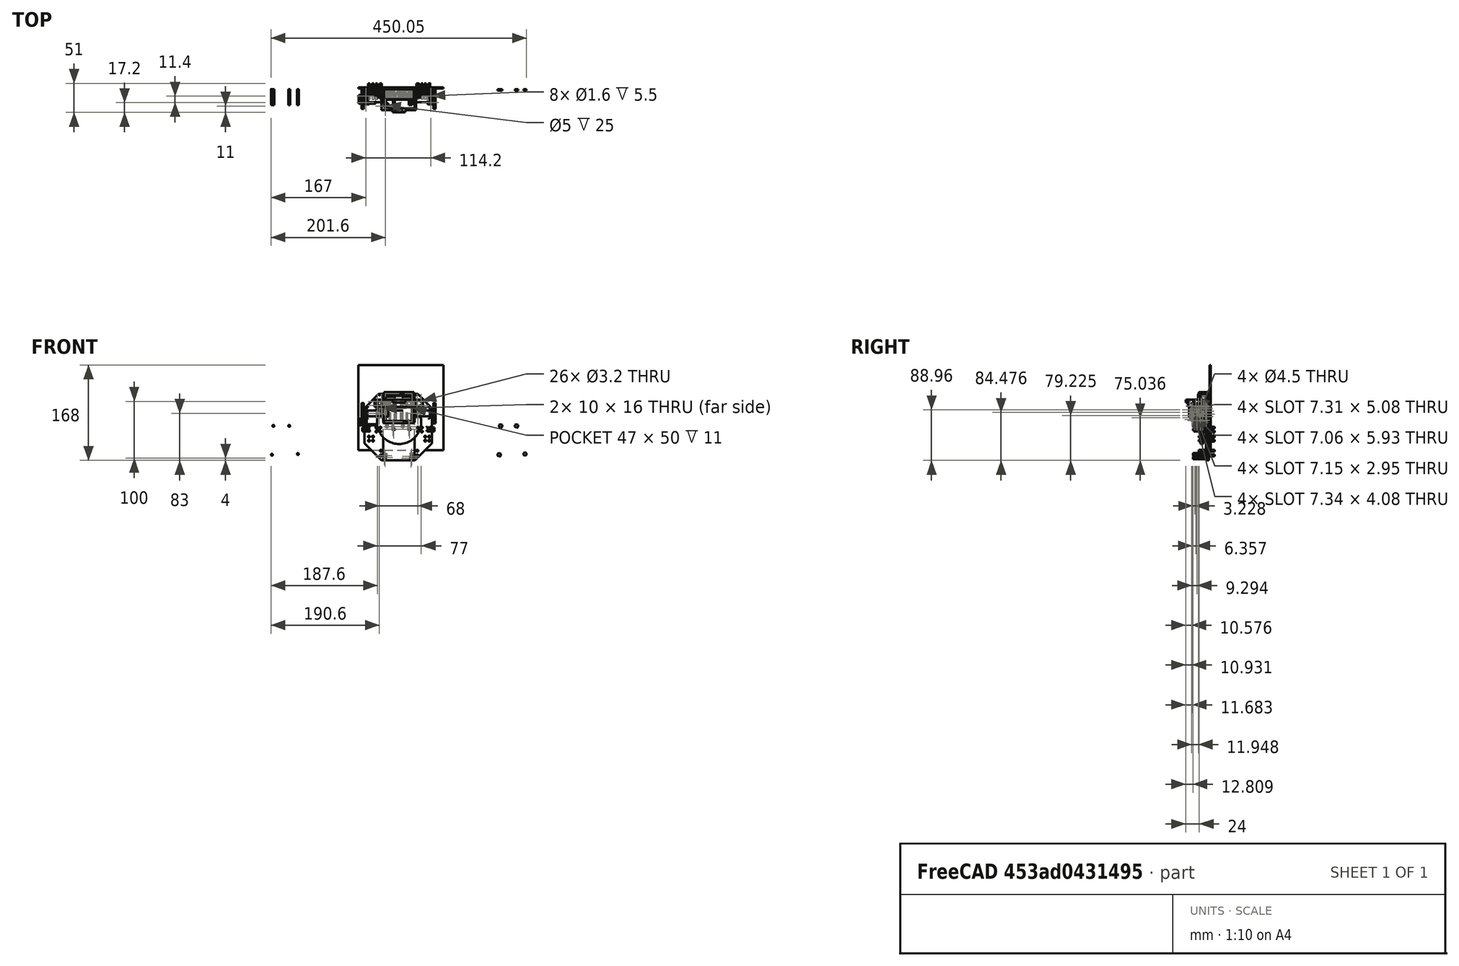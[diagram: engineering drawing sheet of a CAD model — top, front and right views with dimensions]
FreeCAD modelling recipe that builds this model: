
FCSTD DOCUMENT  (FreeCAD 0.16R6712 (Git))
Label: 5028.4 Frank
License: All rights reserved
LicenseURL: http://en.wikipedia.org/wiki/All_rights_reserved
objects: Part::Cylinder×127, Part::Box×74, Part::Cut×71, Part::Fuse×69, Part::Feature×37, Part::MultiFuse×36, Part::Fillet×16, Part::Mirroring×14, Part::Chamfer×12, Part::Cone×8, Part::Compound×3, Part::Torus×2, App::DocumentObjectGroup×1
note: 469 computed .brp shape members not serialized (recipe doc carries the construction recipe); baked Part::Feature solids carry a one-line shape summary decoded from their .brp

FEATURE [Part::Cylinder] Cylinder
  Angle = 360
  Height = 30
  Radius = 7
FEATURE [Part::Cylinder] Cylinder001
  Angle = 360
  Height = 19
  Placement = pos=(0,0,30) rot=(0,0,1;0rad)
  Radius = 7
FEATURE [Part::Cylinder] Cylinder002
  Angle = 360
  Height = 1.8
  Placement = pos=(0,0,49) rot=(0,0,1;0rad)
  Radius = 2.5
FEATURE [Part::Compound] Compound
  Links = -> [Cylinder,Cylinder002,Cylinder001]
FEATURE [Part::Cylinder] Cylinder003
  Angle = 360
  Height = 30
  Radius = 7
FEATURE [Part::Cylinder] Cylinder004
  Angle = 360
  Height = 19
  Placement = pos=(0,0,30) rot=(0,0,1;0rad)
  Radius = 7
FEATURE [Part::Cylinder] Cylinder005
  Angle = 360
  Height = 1.8
  Placement = pos=(0,0,49) rot=(0,0,1;0rad)
  Radius = 2.5
FEATURE [Part::Compound] Compound001
  Links = -> [Cylinder003,Cylinder005,Cylinder004]
  Placement = pos=(14.5,0,50) rot=(1,0,0;3.14159rad)
FEATURE [Part::Cylinder] Cylinder006
  Angle = 360
  Height = 30
  Radius = 7
FEATURE [Part::Cylinder] Cylinder007
  Angle = 360
  Height = 19
  Placement = pos=(0,0,30) rot=(0,0,1;0rad)
  Radius = 7
FEATURE [Part::Cylinder] Cylinder008
  Angle = 360
  Height = 1.8
  Placement = pos=(0,0,49) rot=(0,0,1;0rad)
  Radius = 2.5
FEATURE [Part::Compound] Compound002
  Links = -> [Cylinder006,Cylinder008,Cylinder007]
  Placement = pos=(29,0,0) rot=(0,0,1;0rad)
FEATURE [Part::Box] Box  label="Cube"
  Height = 50
  Length = 47
  Placement = pos=(-9,-8,0) rot=(0,0,1;0rad)
  Width = 12
FEATURE [Part::Box] Box001  label="Cube001"
  Height = 55
  Length = 53
  Placement = pos=(-12,-8,-2.5) rot=(0,0,1;0rad)
  Width = 11
FEATURE [Part::Cylinder] Cylinder009
  Angle = 360
  Height = 50
  Radius = 7
FEATURE [Part::Cylinder] Cylinder010
  Angle = 360
  Height = 50
  Placement = pos=(14.5,0,0) rot=(0,0,1;0rad)
  Radius = 7
FEATURE [Part::Cut] Cut
  Base = -> Box001
  Tool = -> Box
FEATURE [Part::Box] Box002  label="Cube002"
  Height = 55
  Length = 53
  Placement = pos=(-12,3,-2.5) rot=(0,0,1;0rad)
  Width = 7
FEATURE [Part::Fuse] Fusion
  Base = -> Cut
  Tool = -> Box002
FEATURE [Part::Cut] Cut001  label="No idea why this is here...."
  Base = -> Fusion
  Tool = -> Cylinder009
FEATURE [Part::Cylinder] Cylinder011
  Angle = 360
  Height = 50
  Placement = pos=(29,0,0) rot=(0,0,1;0rad)
  Radius = 7
FEATURE [Part::Box] Box003  label="Cube003"
  Height = 5
  Length = 2
  Placement = pos=(28,-9,-2) rot=(0,0,1;0rad)
  Width = 12
FEATURE [Part::Box] Box004  label="Cube004"
  Height = 5
  Length = 2
  Placement = pos=(18.5,-9,46) rot=(0,0,1;0rad)
  Width = 12
FEATURE [Part::Box] Box005  label="Cube005"
  Height = 5
  Length = 2
  Placement = pos=(-2,-9,46) rot=(0,0,1;0rad)
  Width = 12
FEATURE [Part::Box] Box006  label="Cube006"
  Height = 5
  Length = 3
  Placement = pos=(35,-9,-4) rot=(0,0,1;0rad)
  Width = 12
FEATURE [Part::Cut] Cut008
FEATURE [Part::Torus] Torus001
  Angle1 = -180
  Angle2 = 180
  Angle3 = 360
  Placement = pos=(0,0,2) rot=(0,0,1;0rad)
  Radius1 = 19
  Radius2 = 1.5
FEATURE [Part::Cut] Cut009  label="wheel2"
  Base = -> Cut008
  Placement = pos=(75,-7,15) rot=(0,1,0;1.5708rad)
  Tool = -> Torus001
FEATURE [Part::Torus] Torus
  Angle1 = -180
  Angle2 = 180
  Angle3 = 360
  Placement = pos=(0,0,2) rot=(0,0,1;0rad)
  Radius1 = 19
  Radius2 = 1.5
FEATURE [Part::Cut] Cut010
FEATURE [Part::Cut] Cut011  label="wheel1"
  Base = -> Cut010
  Placement = pos=(-51,-7,15) rot=(0,1,0;1.5708rad)
  Tool = -> Torus
FEATURE [Part::Fuse] Fusion003
FEATURE [Part::Cylinder] Cylinder012
  Angle = 360
  Height = 10
  Placement = pos=(5,-4.5,0) rot=(0,1,0;1.5708rad)
  Radius = 0.8
FEATURE [Part::Fuse] Fusion048  label="right-motor001"
  Base = -> Cylinder012
  Placement = pos=(-51,-7,15) rot=(0,0,1;0rad)
  Tool = -> Fusion003
FEATURE [Part::Fuse] Fusion049
FEATURE [Part::Cylinder] Cylinder013
  Angle = 360
  Height = 10
  Placement = pos=(5,-4.5,0) rot=(0,1,0;1.5708rad)
  Radius = 0.8
FEATURE [Part::Fuse] Fusion050  label="left-motor001"
  Base = -> Cylinder013
  Placement = pos=(79,-7,15) rot=(0,0,1;3.14159rad)
  Tool = -> Fusion049
FEATURE [Part::Box] Box007  label="Cube007"
  Height = 5
  Length = 2
  Placement = pos=(37.5,-9,46) rot=(0,0,1;0rad)
  Width = 12
FEATURE [Part::Box] Box008  label="Cube008"
  Height = 5
  Length = 2
  Placement = pos=(8,-9,-2) rot=(0,0,1;0rad)
  Width = 12
FEATURE [Part::Box] Box009  label="The Ground"
  Height = 150
  Length = 150
  Placement = pos=(-57,11,-50) rot=(0,0,1;0rad)
  Width = 2
FEATURE [Part::Box] Box010  label="Motor Mount Left"
  Height = 16
  Length = 4
  Placement = pos=(69,-13,7) rot=(0,0,1;0rad)
  Width = 20
FEATURE [Part::Box] Box011  label="Motor Mount Right"
  Height = 16
  Length = 4
  Placement = pos=(-46,-13,7) rot=(0,0,1;0rad)
  Width = 20
FEATURE [Part::Box] Box012  label="Motor Support Right"
  Height = 16
  Length = 10
  Placement = pos=(-25,-1,7) rot=(0,0,1;0rad)
  Width = 8
FEATURE [Part::Box] Box013  label="Motor Support Left"
  Height = 16
  Length = 10
  Placement = pos=(43,-1,7) rot=(0,0,1;0rad)
  Width = 8
FEATURE [Part::Cylinder] Cylinder014
  Angle = 360
  Height = 28
  Placement = pos=(40.7,0,-10.3) rot=(1,0,0;1.5708rad)
  Radius = 1.6
FEATURE [Part::Cylinder] Cylinder015
  Angle = 360
  Height = 28
  Placement = pos=(-2.4,0,-59.8) rot=(1,0,0;1.5708rad)
  Radius = 1.6
FEATURE [Part::Cylinder] Cylinder016
  Angle = 360
  Height = 28
  Placement = pos=(-5,0,-9) rot=(1,0,0;1.5708rad)
  Radius = 1.6
FEATURE [Part::Cylinder] Cylinder017
  Angle = 360
  Height = 28
  Placement = pos=(25.5,0,-59.8) rot=(1,0,0;1.5708rad)
  Radius = 1.6
FEATURE [Part::Fuse] Fusion051
  Base = -> Cylinder015
  Tool = -> Cylinder016
FEATURE [Part::Fuse] Fusion052
  Base = -> Cylinder014
  Tool = -> Cylinder017
FEATURE [Part::Fuse] Fusion053  label="Screw holes on Arduino Duo"
  Base = -> Fusion051
  Tool = -> Fusion052
FEATURE [Part::Mirroring] Part__Mirroring  label="XXXXXScrew holes on Arduino Duo (Mirror #1)"
  Base = (0,0,0)
  Normal = (0,0,1)
  Placement = pos=(-204,10,-67) rot=(0,0,1;0rad)
  Source = -> Fusion053
FEATURE [Part::Box] Box014  label="Not used Cube"
  Height = 10
  Length = 10
  Placement = pos=(-1,4,-5.85) rot=(0,0,1;0rad)
  Width = 10
FEATURE [Part::Box] Box015  label="Cube014 Arduino Support cube"
  Height = 67
  Length = 55
  Placement = pos=(-13,5,-68) rot=(0,0,1;0rad)
  Width = 5
FEATURE [Part::Cylinder] Cylinder018
  Angle = 360
  Height = 5
  Placement = pos=(15,0,0) rot=(1,0,0;1.5708rad)
  Radius = 39
FEATURE [Part::Cut] Cut014  label="M3 Nut"
  Base = -> Cut001
  Placement = pos=(-6.4,10,-7.2) rot=(1,0,0;1.5708rad)
  Tool = -> Cylinder001
FEATURE [Part::Cut] Cut015  label="M3 Nut001"
  Base = -> Cut001
  Placement = pos=(21.5,10,-7.2) rot=(1,0,0;1.5708rad)
  Tool = -> Cylinder001
FEATURE [Part::Cut] Cut016  label="M3 Nut002"
  Base = -> Cut001
  Placement = pos=(36.7,10,-56.7) rot=(1,0,0;1.5708rad)
  Tool = -> Cylinder001
FEATURE [Part::Cut] Cut017  label="M3 Nut003"
  Base = -> Cut001
  Placement = pos=(-9,10,-58) rot=(1,0,0;1.5708rad)
  Tool = -> Cylinder001
FEATURE [Part::Cut] Cut018
  Base = -> Cut
  Placement = pos=(-9,10,-58) rot=(1,0,0;1.5708rad)
  Tool = -> Box006
FEATURE [Part::Cut] Cut019
  Base = -> Cut
  Placement = pos=(36.7,10,-56.7) rot=(1,0,0;1.5708rad)
  Tool = -> Box006
FEATURE [Part::Cut] Cut020
  Base = -> Cut
  Placement = pos=(-6.4,10,-7.2) rot=(1,0,0;1.5708rad)
  Tool = -> Box006
FEATURE [Part::Cut] Cut021
  Base = -> Cut
  Placement = pos=(21.5,10,-7.2) rot=(1,0,0;1.5708rad)
  Tool = -> Box006
FEATURE [Part::MultiFuse] Fusion054  label="XXXXXHex Holes"
  Placement = pos=(200,0,0) rot=(0,0,1;0rad)
  Shapes = -> [Cut018,Cut021,Cut019,Cut020]
FEATURE [Part::Box] Box016  label="Cube015"
  Height = 117
  Length = 33
  Placement = pos=(-46,7,-68) rot=(0,0,1;0rad)
  Width = 3
FEATURE [Part::Box] Box017  label="Cube016"
  Height = 117
  Length = 31
  Placement = pos=(42,7,-68) rot=(0,0,1;0rad)
  Width = 3
FEATURE [Part::Cylinder] Cylinder019
  Angle = 360
  Height = 28
  Placement = pos=(48,20,-10) rot=(1,0,0;1.5708rad)
  Radius = 1.6
FEATURE [Part::Cylinder] Cylinder020
  Angle = 360
  Height = 28
  Placement = pos=(47,20,-51) rot=(1,0,0;1.5708rad)
  Radius = 1.6
FEATURE [Part::Cylinder] Cylinder021
  Angle = 360
  Height = 28
  Placement = pos=(48,20,-17) rot=(1,0,0;1.5708rad)
  Radius = 1.6
FEATURE [Part::Cylinder] Cylinder022
  Angle = 360
  Height = 28
  Placement = pos=(47,20,-59) rot=(1,0,0;1.5708rad)
  Radius = 1.6
FEATURE [Part::Cylinder] Cylinder023
  Angle = 360
  Height = 28
  Placement = pos=(55,20,-17) rot=(1,0,0;1.5708rad)
  Radius = 1.6
FEATURE [Part::Cylinder] Cylinder024
  Angle = 360
  Height = 28
  Placement = pos=(55,20,-10) rot=(1,0,0;1.5708rad)
  Radius = 1.6
FEATURE [Part::MultiFuse] Fusion055
  Shapes = -> [Cylinder021,Cylinder023,Cylinder024,Cylinder019]
FEATURE [Part::MultiFuse] Fusion056
  Placement = pos=(13,0,-16) rot=(0,0,1;0rad)
  Shapes = -> [Cylinder021,Cylinder023,Cylinder024,Cylinder019]
FEATURE [Part::MultiFuse] Fusion057  label="Mount holes top left"
  Placement = pos=(-1,0,46) rot=(0,0,1;0rad)
  Shapes = -> [Cylinder021,Cylinder023,Cylinder024,Cylinder019]
FEATURE [Part::MultiFuse] Fusion058  label="Mount holes top right"
  Placement = pos=(-71,0,46) rot=(0,0,1;0rad)
  Shapes = -> [Cylinder021,Cylinder023,Cylinder024,Cylinder019]
FEATURE [Part::MultiFuse] Fusion059
  Shapes = -> [Cylinder022,Cylinder020,Fusion055,Fusion056]
FEATURE [Part::Mirroring] Part__Mirroring001  label="Mount holes bottom right"
  Base = (0,0,0)
  Normal = (1,0,0)
  Placement = pos=(30,0,0) rot=(0,0,1;0rad)
  Source = -> Fusion059
FEATURE [Part::Cylinder] Cylinder025
  Angle = 360
  Height = 28
  Placement = pos=(48,20,-10) rot=(1,0,0;1.5708rad)
  Radius = 1.6
FEATURE [Part::Cylinder] Cylinder026
  Angle = 360
  Height = 28
  Placement = pos=(47,20,-51) rot=(1,0,0;1.5708rad)
  Radius = 1.6
FEATURE [Part::Cylinder] Cylinder027
  Angle = 360
  Height = 28
  Placement = pos=(48,20,-17) rot=(1,0,0;1.5708rad)
  Radius = 1.6
FEATURE [Part::Cylinder] Cylinder028
  Angle = 360
  Height = 28
  Placement = pos=(47,20,-59) rot=(1,0,0;1.5708rad)
  Radius = 1.6
FEATURE [Part::Cylinder] Cylinder029
  Angle = 360
  Height = 28
  Placement = pos=(55,20,-17) rot=(1,0,0;1.5708rad)
  Radius = 1.6
FEATURE [Part::Cylinder] Cylinder030
  Angle = 360
  Height = 28
  Placement = pos=(55,20,-10) rot=(1,0,0;1.5708rad)
  Radius = 1.6
FEATURE [Part::MultiFuse] Fusion060
  Shapes = -> [Cylinder027,Cylinder029,Cylinder030,Cylinder025]
FEATURE [Part::MultiFuse] Fusion061
  Placement = pos=(13,0,-16) rot=(0,0,1;0rad)
  Shapes = -> [Cylinder027,Cylinder029,Cylinder030,Cylinder025]
FEATURE [Part::MultiFuse] Fusion062  label="Mount holes bottom left"
  Shapes = -> [Cylinder028,Cylinder026,Fusion060,Fusion061]
FEATURE [Part::Cylinder] Cylinder031  label="Cylinder127"
  Angle = 360
  Height = 10
  Placement = pos=(0,18,29) rot=(0,0,1;0rad)
  Radius = 2.25
FEATURE [Part::Cylinder] Cylinder032  label="Cylinder128"
  Angle = 360
  Height = 10
  Placement = pos=(4.5,18,32) rot=(0,0,1;0rad)
  Radius = 1
FEATURE [Part::Cylinder] Cylinder033  label="Cylinder129"
  Angle = 360
  Height = 10
  Placement = pos=(-4.5,18,32) rot=(0,0,1;0rad)
  Radius = 1
FEATURE [Part::Fuse] Fusion009  label="Mounting Screw Holes"
  Base = -> Cylinder032
  Tool = -> Cylinder033
FEATURE [Part::Fuse] Fusion071  label="Motor Holes Left"
  Base = -> Cylinder031
  Placement = pos=(37,-7,-3) rot=(0.57735,0.57735,0.57735;2.0944rad)
  Tool = -> Fusion009
FEATURE [Part::Cylinder] Cylinder034  label="Cylinder130"
  Angle = 360
  Height = 10
  Placement = pos=(0,18,29) rot=(0,0,1;0rad)
  Radius = 2.25
FEATURE [Part::Cylinder] Cylinder035  label="Cylinder131"
  Angle = 360
  Height = 10
  Placement = pos=(4.5,18,32) rot=(0,0,1;0rad)
  Radius = 1
FEATURE [Part::Cylinder] Cylinder036  label="Cylinder132"
  Angle = 360
  Height = 10
  Placement = pos=(-4.5,18,32) rot=(0,0,1;0rad)
  Radius = 1
FEATURE [Part::Fuse] Fusion072  label="Mounting Screw Holes001"
  Base = -> Cylinder035
  Tool = -> Cylinder036
FEATURE [Part::Fuse] Fusion073  label="Motor Holes Right"
  Base = -> Cylinder034
  Placement = pos=(-79,-7,-3) rot=(0.57735,0.57735,0.57735;2.0944rad)
  Tool = -> Fusion072
FEATURE [Part::Cylinder] Cylinder037  label="Cylinder133"
  Angle = 360
  Height = 28
  Placement = pos=(40.7,0,-10.3) rot=(1,0,0;1.5708rad)
  Radius = 1.6
FEATURE [Part::Cylinder] Cylinder038  label="Cylinder134"
  Angle = 360
  Height = 28
  Placement = pos=(-2.4,0,-59.8) rot=(1,0,0;1.5708rad)
  Radius = 1.6
FEATURE [Part::Cylinder] Cylinder039  label="Cylinder135"
  Angle = 360
  Height = 28
  Placement = pos=(-5,0,-9) rot=(1,0,0;1.5708rad)
  Radius = 1.6
FEATURE [Part::Cylinder] Cylinder040  label="Cylinder136"
  Angle = 360
  Height = 28
  Placement = pos=(25.5,0,-59.8) rot=(1,0,0;1.5708rad)
  Radius = 1.6
FEATURE [Part::Fuse] Fusion074
  Base = -> Cylinder038
  Tool = -> Cylinder039
FEATURE [Part::Fuse] Fusion075
  Base = -> Cylinder037
  Tool = -> Cylinder040
FEATURE [Part::Fuse] Fusion076  label="Screw holes on Arduino Duo001"
  Base = -> Fusion074
  Tool = -> Fusion075
FEATURE [Part::Mirroring] Part__Mirroring002  label="Screw holes on Arduino Duo (Mirror #1)001"
  Base = (0,0,0)
  Normal = (0,0,1)
  Placement = pos=(-4,10,-67) rot=(0,0,1;0rad)
  Source = -> Fusion076
FEATURE [Part::Mirroring] Part__Mirroring003  label="Screw holes on Arduino Duo (Mirror #1)001 (Mirror #4)"
  Base = (0,0,0)
  Normal = (1,0,0)
  Placement = pos=(27,0,-6) rot=(0,0,1;0rad)
  Source = -> Part__Mirroring002
FEATURE [Part::Box] Box018  label="Cube017"
  Height = 50
  Length = 47
  Placement = pos=(-9,-8,0) rot=(0,0,1;0rad)
  Width = 12
FEATURE [Part::Box] Box019  label="Cube018"
  Height = 55
  Length = 53
  Placement = pos=(-12,-8,-2.5) rot=(0,0,1;0rad)
  Width = 11
FEATURE [Part::Cut] Cut031
  Base = -> Box019
  Tool = -> Box018
FEATURE [Part::Box] Box020  label="Cube019"
  Height = 5
  Length = 3
  Placement = pos=(35,-9,-4) rot=(0,0,1;0rad)
  Width = 12
FEATURE [Part::Cut] Cut032
  Base = -> Cut031
  Placement = pos=(-9,10,-58) rot=(1,0,0;1.5708rad)
  Tool = -> Box020
FEATURE [Part::Cut] Cut033
  Base = -> Cut031
  Placement = pos=(36.7,10,-56.7) rot=(1,0,0;1.5708rad)
  Tool = -> Box020
FEATURE [Part::Cut] Cut034
  Base = -> Cut031
  Placement = pos=(-6.4,10,-7.2) rot=(1,0,0;1.5708rad)
  Tool = -> Box020
FEATURE [Part::Cut] Cut035
  Base = -> Cut031
  Placement = pos=(21.5,10,-7.2) rot=(1,0,0;1.5708rad)
  Tool = -> Box020
FEATURE [Part::MultiFuse] Fusion077
  Shapes = -> [Cut032,Cut035,Cut033,Cut034]
FEATURE [Part::Mirroring] Part__Mirroring004  label="Hex Holes"
  Base = (0,0,0)
  Normal = (1,0,0)
  Placement = pos=(27,0,-6) rot=(0,0,1;0rad)
  Source = -> Fusion077
FEATURE [Part::Box] Box021  label="Cube020"
  Height = 13
  Length = 61
  Placement = pos=(-16,-27,26) rot=(0,0,1;0rad)
  Width = 34
FEATURE [Part::Box] Box022  label="Cube021"
  Height = 13
  Length = 12
  Placement = pos=(45,4,26) rot=(0,0,1;0rad)
  Width = 3
FEATURE [Part::Box] Box023  label="Cube022"
  Height = 13
  Length = 12
  Placement = pos=(-28,4,26) rot=(0,0,1;0rad)
  Width = 3
FEATURE [Part::Box] Box024  label="Cube023"
  Height = 13
  Length = 55
  Placement = pos=(-13,-24,26) rot=(0,0,1;0rad)
  Width = 31
FEATURE [Part::Cylinder] Cylinder041  label="Cylinder137"
  Angle = 360
  Height = 28
  Placement = pos=(54,20,29) rot=(1,0,0;1.5708rad)
  Radius = 1.6
FEATURE [Part::Cylinder] Cylinder042  label="Cylinder138"
  Angle = 360
  Height = 28
  Placement = pos=(54,20,36) rot=(1,0,0;1.5708rad)
  Radius = 1.6
FEATURE [Part::Cylinder] Cylinder043  label="Cylinder139"
  Angle = 360
  Height = 28
  Placement = pos=(-23,20,29) rot=(1,0,0;1.5708rad)
  Radius = 1.6
FEATURE [Part::Cylinder] Cylinder044  label="Cylinder140"
  Angle = 360
  Height = 28
  Placement = pos=(-23,20,36) rot=(1,0,0;1.5708rad)
  Radius = 1.6
FEATURE [Part::Cylinder] Cylinder045  label="Cylinder141"
  Angle = 360
  Height = 10
  Placement = pos=(36,-17.25,32.5) rot=(0,1,0;1.5708rad)
  Radius = 2.5
FEATURE [Part::Cut] Cut037
  Base = -> Box021
  Tool = -> Box024
FEATURE [Part::Cut] Cut038
  Base = -> Cut037
  Tool = -> Cylinder045
FEATURE [Part::Box] Box025  label="Cube024"
  Height = 5
  Length = 22
  Placement = pos=(3.5,-31,34) rot=(0,0,1;0rad)
  Width = 4
FEATURE [Part::Cylinder] Cylinder046  label="Cylinder142"
  Angle = 360
  Height = 10
  Placement = pos=(20.75,-29,30) rot=(0,0,1;0rad)
  Radius = 0.85
FEATURE [Part::Cylinder] Cylinder047  label="Cylinder143"
  Angle = 360
  Height = 10
  Placement = pos=(8.25,-29,40) rot=(1,0,0;3.14159rad)
  Radius = 0.85
FEATURE [Part::Fuse] Fusion078
  Base = -> Cylinder046
  Tool = -> Cylinder047
FEATURE [Part::Cut] Cut039
  Base = -> Box025
  Tool = -> Fusion078
FEATURE [Part::Fuse] Fusion079
  Base = -> Cut038
  Tool = -> Cut039
FEATURE [Part::Fuse] Fusion080
  Base = -> Cylinder043
  Tool = -> Cylinder044
FEATURE [Part::Fuse] Fusion081
  Base = -> Cylinder041
  Tool = -> Cylinder042
FEATURE [Part::Fuse] Fusion082
  Base = -> Box023
  Tool = -> Fusion079
FEATURE [Part::Fuse] Fusion083
  Base = -> Box022
  Tool = -> Fusion082
FEATURE [Part::Cut] Cut040
  Base = -> Fusion083
  Tool = -> Fusion081
FEATURE [Part::Cut] Cut041  label="Switch Bracket"
  Base = -> Cut040
  Tool = -> Fusion080
FEATURE [Part::Cylinder] Cylinder048  label="Cylinder144"
  Angle = 360
  Height = 28
  Placement = pos=(-23,20,29) rot=(1,0,0;1.5708rad)
  Radius = 1.6
FEATURE [Part::Cylinder] Cylinder049  label="Cylinder145"
  Angle = 360
  Height = 28
  Placement = pos=(-23,20,36) rot=(1,0,0;1.5708rad)
  Radius = 1.6
FEATURE [Part::Fuse] Fusion084
  Base = -> Cylinder048
  Placement = pos=(1,0,0) rot=(0,0,1;0rad)
  Tool = -> Cylinder049
FEATURE [Part::Cylinder] Cylinder050  label="Cylinder146"
  Angle = 360
  Height = 28
  Placement = pos=(-23,20,29) rot=(1,0,0;1.5708rad)
  Radius = 1.6
FEATURE [Part::Cylinder] Cylinder051  label="Cylinder147"
  Angle = 360
  Height = 28
  Placement = pos=(-23,20,36) rot=(1,0,0;1.5708rad)
  Radius = 1.6
FEATURE [Part::Fuse] Fusion085
  Base = -> Cylinder050
  Placement = pos=(-1,0,0) rot=(0,0,1;0rad)
  Tool = -> Cylinder051
FEATURE [Part::Cut] Cut042
  Base = -> Cut041
  Tool = -> Fusion084
FEATURE [Part::Cut] Cut043  label="Switch Bracket001"
  Base = -> Cut042
  Tool = -> Fusion085
FEATURE [Part::Cylinder] Cylinder052  label="Cylinder148"
  Angle = 360
  Height = 42
  Radius = 4.8
FEATURE [Part::Cylinder] Cylinder053  label="Cylinder149"
  Angle = 360
  Height = 1.6
  Placement = pos=(0,0,42) rot=(0,0,1;0rad)
  Radius = 1.65
FEATURE [Part::Fuse] Fusion086
  Base = -> Cylinder052
  Placement = pos=(2,0,0) rot=(0,0,1;0rad)
  Tool = -> Cylinder053
FEATURE [Part::Cylinder] Cylinder054  label="Cylinder150"
  Angle = 360
  Height = 42
  Radius = 4.8
FEATURE [Part::Cylinder] Cylinder055  label="Cylinder151"
  Angle = 360
  Height = 1.6
  Placement = pos=(0,0,42) rot=(0,0,1;0rad)
  Radius = 1.65
FEATURE [Part::Fuse] Fusion087
  Base = -> Cylinder054
  Placement = pos=(12,0,0) rot=(0,0,1;0rad)
  Tool = -> Cylinder055
FEATURE [Part::Cylinder] Cylinder056  label="Cylinder152"
  Angle = 360
  Height = 42
  Radius = 4.8
FEATURE [Part::Cylinder] Cylinder057  label="Cylinder153"
  Angle = 360
  Height = 1.6
  Placement = pos=(0,0,42) rot=(0,0,1;0rad)
  Radius = 1.65
FEATURE [Part::Fuse] Fusion088
  Base = -> Cylinder056
  Placement = pos=(22,0,0) rot=(0,0,1;0rad)
  Tool = -> Cylinder057
FEATURE [Part::Cylinder] Cylinder058  label="Cylinder154"
  Angle = 360
  Height = 42
  Radius = 4.8
FEATURE [Part::Cylinder] Cylinder059  label="Cylinder155"
  Angle = 360
  Height = 1.6
  Placement = pos=(0,0,42) rot=(0,0,1;0rad)
  Radius = 1.65
FEATURE [Part::Fuse] Fusion089
  Base = -> Cylinder058
  Placement = pos=(32,0,0) rot=(0,0,1;0rad)
  Tool = -> Cylinder059
FEATURE [Part::Cylinder] Cylinder060  label="Cylinder156"
  Angle = 360
  Height = 42
  Radius = 4.8
FEATURE [Part::Cylinder] Cylinder061  label="Cylinder157"
  Angle = 360
  Height = 1.6
  Placement = pos=(0,0,42) rot=(0,0,1;0rad)
  Radius = 1.65
FEATURE [Part::Fuse] Fusion093
  Base = -> Cylinder060
  Placement = pos=(-8,0,0) rot=(0,0,1;0rad)
  Tool = -> Cylinder061
FEATURE [Part::MultiFuse] Fusion094  label="AAA Batts"
  Placement = pos=(2.5,0,2) rot=(0,0,1;0rad)
  Shapes = -> [Fusion093,Fusion086,Fusion087,Fusion088,Fusion089]
FEATURE [Part::Cylinder] Cylinder062  label="Cylinder158"
  Angle = 360
  Height = 10
  Radius = 17
FEATURE [Part::Cylinder] Cylinder063  label="Cylinder159"
  Angle = 360
  Height = 16
  Placement = pos=(0,0,-4) rot=(0,0,1;0rad)
  Radius = 10
FEATURE [Part::Cut] Cut044
  Base = -> Cylinder062
  Tool = -> Cylinder063
FEATURE [Part::Box] Box026  label="Cube025"
  Height = 20
  Length = 18
  Placement = pos=(0,0,-5) rot=(0,0,1;0rad)
  Width = 20
FEATURE [Part::Box] Box027  label="Cube026"
  Height = 20
  Length = 10
  Placement = pos=(0,0,-5) rot=(0,0,1;0.174533rad)
  Width = 20
FEATURE [Part::Cut] Cut045
  Base = -> Box027
  Tool = -> Box026
FEATURE [Part::Feature] Cut045001
  Placement = pos=(0,0,0) rot=(0,0,1;0.349066rad)
  shape: bbox 10 x 22.32 x 20 mm, 7 faces (baked)
FEATURE [Part::Feature] Cut045002
  Placement = pos=(0,0,0) rot=(0,0,1;0.698132rad)
  shape: bbox 15.32 x 20.52 x 20 mm, 7 faces (baked)
FEATURE [Part::Feature] Cut045003
  Placement = pos=(0,0,0) rot=(0,0,1;1.0472rad)
  shape: bbox 18.79 x 16.24 x 20 mm, 7 faces (baked)
FEATURE [Part::Feature] Cut045004
  Placement = pos=(0,0,0) rot=(0,0,1;1.39626rad)
  shape: bbox 20 x 10 x 20 mm, 7 faces (baked)
FEATURE [Part::Feature] Cut045005
  Placement = pos=(0,0,0) rot=(0,0,1;1.74533rad)
  shape: bbox 22.21 x 9.894 x 20 mm, 7 faces (baked)
FEATURE [Part::Feature] Cut045006
  Placement = pos=(0,0,0) rot=(0,0,1;2.0944rad)
  shape: bbox 21.75 x 12.86 x 20 mm, 7 faces (baked)
FEATURE [Part::Feature] Cut045007
  Placement = pos=(0,0,0) rot=(0,0,1;2.44346rad)
  shape: bbox 18.66 x 17.32 x 20 mm, 7 faces (baked)
FEATURE [Part::Feature] Cut045008
  Placement = pos=(0,0,0) rot=(0,0,1;2.79253rad)
  shape: bbox 13.32 x 19.7 x 20 mm, 7 faces (baked)
FEATURE [Part::Feature] Cut045009
  Placement = pos=(0,0,0) rot=(0,0,1;3.14159rad)
  shape: bbox 10.1 x 21.43 x 20 mm, 7 faces (baked)
FEATURE [Part::Feature] Cut045010
  Placement = pos=(0,0,0) rot=(0,0,1;3.49066rad)
  shape: bbox 10 x 22.32 x 20 mm, 7 faces (baked)
FEATURE [Part::Feature] Cut045011
  Placement = pos=(0,0,0) rot=(0,0,1;3.83972rad)
  shape: bbox 15.32 x 20.52 x 20 mm, 7 faces (baked)
FEATURE [Part::Feature] Cut045012
  Placement = pos=(0,0,0) rot=(0,0,1;4.18879rad)
  shape: bbox 18.79 x 16.24 x 20 mm, 7 faces (baked)
FEATURE [Part::Feature] Cut045013
  Placement = pos=(0,0,0) rot=(0,0,-1;1.74533rad)
  shape: bbox 20 x 10 x 20 mm, 7 faces (baked)
FEATURE [Part::Feature] Cut045014
  Placement = pos=(0,0,0) rot=(0,0,-1;1.39626rad)
  shape: bbox 22.21 x 9.894 x 20 mm, 7 faces (baked)
FEATURE [Part::Feature] Cut045015
  Placement = pos=(0,0,0) rot=(0,0,-1;1.0472rad)
  shape: bbox 21.75 x 12.86 x 20 mm, 7 faces (baked)
FEATURE [Part::Feature] Cut045016
  Placement = pos=(0,0,0) rot=(0,0,-1;0.698132rad)
  shape: bbox 18.66 x 17.32 x 20 mm, 7 faces (baked)
FEATURE [Part::Feature] Cut045017
  Placement = pos=(0,0,0) rot=(0,0,-1;0.349066rad)
  shape: bbox 13.32 x 19.7 x 20 mm, 7 faces (baked)
FEATURE [Part::MultiFuse] Fusion095
  Shapes = -> [Cut045001,Cut045008,Cut045010,Cut045009,Cut045005,Cut045003,Cut045006,Cut045002,Cut045004,Cut045007,Cut045016,Cut045017,Cut045011,Cut045012,Cut045013,Cut045014,Cut045015,Cut045]
FEATURE [Part::Cut] Cut045018
  Base = -> Cut044
  Placement = pos=(72,-7,15) rot=(0,1,0;1.5708rad)
  Tool = -> Fusion095
FEATURE [Part::Cut] Cut045019  label="Wheel with Spokes AB"
  Base = -> Cut009
  Tool = -> Cut045018
FEATURE [Part::Box] Box028  label="Cube027"
  Height = 5
  Length = 2
  Placement = pos=(37.5,-9,-2) rot=(0,0,1;0rad)
  Width = 12
FEATURE [Part::Box] Box029  label="Cube028"
  Height = 50
  Length = 47
  Placement = pos=(-9,-8,0) rot=(0,0,1;0rad)
  Width = 12
FEATURE [Part::Box] Box030  label="Cube029"
  Height = 55
  Length = 53
  Placement = pos=(-12,-8,-2.5) rot=(0,0,1;0rad)
  Width = 11
FEATURE [Part::Cylinder] Cylinder064  label="Cylinder160"
  Angle = 360
  Height = 50
  Radius = 7
FEATURE [Part::Cut] Cut045020
  Base = -> Box030
  Tool = -> Box029
FEATURE [Part::Box] Box031  label="Cube030"
  Height = 55
  Length = 53
  Placement = pos=(-12,3,-2.5) rot=(0,0,1;0rad)
  Width = 7
FEATURE [Part::Fuse] Fusion096
  Base = -> Cut045020
  Tool = -> Box031
FEATURE [Part::Box] Box032  label="Battery Base"
  Height = 50
  Length = 55
  Placement = pos=(-13,3,-1) rot=(0,0,1;0rad)
  Width = 7
FEATURE [Part::Box] Box033  label="Cube031"
  Height = 30
  Length = 10
  Placement = pos=(-14,-25,9) rot=(0,0,1;0rad)
  Width = 10
FEATURE [Part::Cylinder] Cylinder065  label="Cylinder161"
  Angle = 360
  Height = 43.5
  Placement = pos=(4,0,2) rot=(0,0,1;0rad)
  Radius = 4.8
FEATURE [Part::Cylinder] Cylinder066  label="Cylinder162"
  Angle = 360
  Height = 1.6
  Placement = pos=(4,0,44) rot=(0,0,1;0rad)
  Radius = 1.65
FEATURE [Part::Fuse] Fusion097
  Base = -> Cylinder065
  Tool = -> Cylinder066
FEATURE [Part::Cylinder] Cylinder067  label="Cylinder163"
  Angle = 360
  Height = 43.5
  Placement = pos=(14,0,2) rot=(0,0,1;0rad)
  Radius = 4.8
FEATURE [Part::Cylinder] Cylinder068  label="Cylinder164"
  Angle = 360
  Height = 1.6
  Placement = pos=(14,0,44) rot=(0,0,1;0rad)
  Radius = 1.65
FEATURE [Part::Fuse] Fusion098
  Base = -> Cylinder067
  Tool = -> Cylinder068
FEATURE [Part::Cylinder] Cylinder069  label="Cylinder165"
  Angle = 360
  Height = 43.5
  Placement = pos=(24,0,2) rot=(0,0,1;0rad)
  Radius = 4.8
FEATURE [Part::Cylinder] Cylinder070  label="Cylinder166"
  Angle = 360
  Height = 1.6
  Placement = pos=(24,0,44) rot=(0,0,1;0rad)
  Radius = 1.65
FEATURE [Part::Fuse] Fusion099
  Base = -> Cylinder069
  Tool = -> Cylinder070
FEATURE [Part::Cylinder] Cylinder071  label="Cylinder167"
  Angle = 360
  Height = 43.5
  Placement = pos=(34,0,2) rot=(0,0,1;0rad)
  Radius = 4.8
FEATURE [Part::Cylinder] Cylinder072  label="Cylinder168"
  Angle = 360
  Height = 1.6
  Placement = pos=(34,0,44) rot=(0,0,1;0rad)
  Radius = 1.65
FEATURE [Part::Fuse] Fusion100
  Base = -> Cylinder071
  Tool = -> Cylinder072
FEATURE [Part::Cylinder] Cylinder073  label="Cylinder169"
  Angle = 360
  Height = 43.5
  Placement = pos=(-6,0,2) rot=(0,0,1;0rad)
  Radius = 4.8
FEATURE [Part::Cylinder] Cylinder074  label="Cylinder170"
  Angle = 360
  Height = 1.6
  Placement = pos=(-6,0,44) rot=(0,0,1;0rad)
  Radius = 1.65
FEATURE [Part::Fuse] Fusion101
  Base = -> Cylinder073
  Tool = -> Cylinder074
FEATURE [Part::MultiFuse] Fusion102  label="AAA Batts001"
  Shapes = -> [Fusion101,Fusion097,Fusion098,Fusion099,Fusion100]
FEATURE [Part::Cylinder] Cylinder075  label="Cylinder171"
  Angle = 360
  Height = 10
  Placement = pos=(-9,-20,4) rot=(0,0,1;0rad)
  Radius = 2.75
FEATURE [Part::Cylinder] Cylinder076  label="Cylinder172"
  Angle = 360
  Height = 27
  Placement = pos=(-9,-20,14) rot=(0,0,1;0rad)
  Radius = 2.5
FEATURE [Part::Fuse] Fusion103  label="phototransistor hole"
  Base = -> Cylinder075
  Tool = -> Cylinder076
FEATURE [Part::Cut] Cut045021  label="Phototransistor holder"
  Base = -> Box033
  Tool = -> Fusion103
FEATURE [Part::Fuse] Fusion104  label="Switch Mount with phototransistor hole"
  Base = -> Cut043
  Tool = -> Cut045021
FEATURE [Part::Cut] Cut045022
  Base = -> Box032
  Tool = -> Fusion102
FEATURE [Part::Box] Box034  label="Cube032"
  Height = 2.5
  Length = 55
  Placement = pos=(-13,-9,-1) rot=(0,0,1;0rad)
  Width = 12
FEATURE [Part::Box] Box035  label="Cube033"
  Height = 2.5
  Length = 55
  Placement = pos=(-13,-9,46.5) rot=(0,0,1;0rad)
  Width = 12
FEATURE [Part::Box] Box036  label="Cube034"
  Height = 50
  Length = 2.5
  Placement = pos=(-13,-9,-1) rot=(0,0,1;0rad)
  Width = 12
FEATURE [Part::Box] Box037  label="Cube035"
  Height = 50
  Length = 2.5
  Placement = pos=(39.5,-9,-1) rot=(0,0,1;0rad)
  Width = 12
FEATURE [Part::MultiFuse] Fusion105
  Shapes = -> [Box034,Box036,Box037,Box035]
FEATURE [Part::Box] Box038  label="Cube036"
  Height = 5
  Length = 2
  Placement = pos=(-10.5,-9,46) rot=(0,0,1;0rad)
  Width = 12
FEATURE [Part::Box] Box039  label="Cube037"
  Height = 5
  Length = 2
  Placement = pos=(-10.5,-9,-2) rot=(0,0,1;0rad)
  Width = 12
FEATURE [Part::MultiFuse] Fusion106
  Shapes = -> [Box039,Box038,Box028,Box007]
FEATURE [Part::MultiFuse] Fusion107
  Shapes = -> [Box003,Box004,Box005,Box008]
FEATURE [Part::Cut] Cut045023
  Base = -> Fusion105
  Tool = -> Fusion106
FEATURE [Part::Cut] Cut045024
  Base = -> Cut045023
  Tool = -> Fusion107
FEATURE [Part::Box] Box040  label="Cube038"
  Height = 1.6
  Length = 30
  Placement = pos=(-56,-15.5,-6) rot=(0,0,1;0rad)
  Width = 15
FEATURE [Part::Box] Box041  label="Cube039"
  Height = 10
  Length = 14
  Placement = pos=(-56,-10.5,-4.5) rot=(0,0,1;0rad)
  Width = 6
FEATURE [Part::Box] Box042  label="Cube040"
  Height = 10
  Length = 5.3
  Placement = pos=(-51.7,-11.5,-4.5) rot=(0,0,1;0rad)
  Width = 8
FEATURE [Part::Cut] Cut045025
  Base = -> Box041
  Tool = -> Box042
FEATURE [Part::Fuse] Fusion108  label="Spoke Sensor PCB"
  Base = -> Box040
  Tool = -> Cut045025
FEATURE [Part::Cylinder] Cylinder077  label="Cylinder173"
  Angle = 360
  Height = 14.5
  Placement = pos=(-43.6,-2.4,-9) rot=(0,0,1;0rad)
  Radius = 0.8
FEATURE [Part::Cylinder] Cylinder078  label="Cylinder174"
  Angle = 360
  Height = 14.5
  Placement = pos=(-43.6,-13.8,-9) rot=(0,0,1;0rad)
  Radius = 0.8
FEATURE [Part::Fuse] Fusion109
  Base = -> Cylinder077
  Tool = -> Cylinder078
FEATURE [Part::Cut] Cut045026  label="Spoke Sensor PCB001"
  Base = -> Fusion108
  Tool = -> Fusion109
FEATURE [Part::Cylinder] Cylinder079  label="Cylinder175"
  Angle = 360
  Height = 14.5
  Placement = pos=(-43.6,-2.4,-18) rot=(0,0,1;0rad)
  Radius = 0.8
FEATURE [Part::Cylinder] Cylinder080  label="Cylinder176"
  Angle = 360
  Height = 14.5
  Placement = pos=(-43.6,-13.8,-18) rot=(0,0,1;0rad)
  Radius = 0.8
FEATURE [Part::Fuse] Fusion110  label="Batt Holder"
  Base = -> Cut045022
  Tool = -> Cut045024
FEATURE [Part::Box] Box043  label="Cube041"
  Height = 4
  Length = 12
  Placement = pos=(-50,-16.75,-17) rot=(0,0,1;0rad)
  Width = 26.75
FEATURE [Part::Chamfer] Chamfer
  Base = -> Box043
  Edges = 1 edges r=7: [Edge3]
FEATURE [Part::Cone] Cone
  Angle = 360
  Height = 1.5
  Placement = pos=(-43.6,-2.4,-13) rot=(0,0,1;0rad)
  Radius1 = 2.75
  Radius2 = 1.25
FEATURE [Part::Cone] Cone001
  Angle = 360
  Height = 1.5
  Placement = pos=(-43.6,-13.8,-13) rot=(0,0,1;0rad)
  Radius1 = 2.75
  Radius2 = 1.25
FEATURE [Part::Fuse] Fusion111
  Base = -> Cone
  Tool = -> Cone001
FEATURE [Part::Fuse] Fusion112
  Base = -> Chamfer
  Tool = -> Fusion111
FEATURE [Part::Fuse] Fusion113
  Base = -> Cylinder079
  Tool = -> Cylinder080
FEATURE [Part::Cut] Cut045027
  Base = -> Fusion112
  Tool = -> Fusion113
FEATURE [Part::Cylinder] Cylinder081  label="Cylinder177"
  Angle = 360
  Height = 14.5
  Placement = pos=(-43.6,-2.4,-18) rot=(0,0,1;0rad)
  Radius = 0.8
FEATURE [Part::Cylinder] Cylinder082  label="Cylinder178"
  Angle = 360
  Height = 14.5
  Placement = pos=(-43.6,-13.8,-18) rot=(0,0,1;0rad)
  Radius = 0.8
FEATURE [Part::Box] Box044  label="Cube042"
  Height = 4
  Length = 12
  Placement = pos=(-50,-16.75,-17) rot=(0,0,1;0rad)
  Width = 26.75
FEATURE [Part::Chamfer] Chamfer001
  Base = -> Box044
  Edges = 1 edges r=7: [Edge3]
FEATURE [Part::Cone] Cone002
  Angle = 360
  Height = 1.5
  Placement = pos=(-43.6,-2.4,-13) rot=(0,0,1;0rad)
  Radius1 = 2.75
  Radius2 = 1.25
FEATURE [Part::Cone] Cone003
  Angle = 360
  Height = 1.5
  Placement = pos=(-43.6,-13.8,-13) rot=(0,0,1;0rad)
  Radius1 = 2.75
  Radius2 = 1.25
FEATURE [Part::Fuse] Fusion114
  Base = -> Cone002
  Tool = -> Cone003
FEATURE [Part::Fuse] Fusion115
  Base = -> Chamfer001
  Tool = -> Fusion114
FEATURE [Part::Fuse] Fusion116
  Base = -> Cylinder081
  Tool = -> Cylinder082
FEATURE [Part::Cut] Cut045028
  Base = -> Fusion115
  Tool = -> Fusion116
FEATURE [Part::Mirroring] Part__Mirroring005  label="Cut045028 (Mirror #6)"
  Base = (0,0,0)
  Normal = (1,0,0)
  Placement = pos=(27,0,0) rot=(0,0,1;0rad)
  Source = -> Cut045028
FEATURE [Part::Box] Box045  label="Cube043"
  Height = 5
  Length = 2
  Placement = pos=(28,-9,-2) rot=(0,0,1;0rad)
  Width = 12
FEATURE [Part::Box] Box046  label="Cube044"
  Height = 5
  Length = 2
  Placement = pos=(18.5,-9,46) rot=(0,0,1;0rad)
  Width = 12
FEATURE [Part::Box] Box047  label="Cube045"
  Height = 5
  Length = 2
  Placement = pos=(-2,-9,46) rot=(0,0,1;0rad)
  Width = 12
FEATURE [Part::Box] Box048  label="Cube046"
  Height = 5
  Length = 2
  Placement = pos=(37.5,-9,46) rot=(0,0,1;0rad)
  Width = 12
FEATURE [Part::Box] Box049  label="Cube047"
  Height = 5
  Length = 2
  Placement = pos=(8,-9,-2) rot=(0,0,1;0rad)
  Width = 12
FEATURE [Part::Box] Box050  label="Motor Mount Left001"
  Height = 16
  Length = 4
  Placement = pos=(69,-13,7) rot=(0,0,1;0rad)
  Width = 20
FEATURE [Part::Box] Box051  label="Motor Mount Right001"
  Height = 16
  Length = 4
  Placement = pos=(-46,-13,7) rot=(0,0,1;0rad)
  Width = 20
FEATURE [Part::Box] Box052  label="Motor Support Right001"
  Height = 16
  Length = 10
  Placement = pos=(-25,-1,7) rot=(0,0,1;0rad)
  Width = 8
FEATURE [Part::Box] Box053  label="Motor Support Left001"
  Height = 16
  Length = 10
  Placement = pos=(43,-1,7) rot=(0,0,1;0rad)
  Width = 8
FEATURE [Part::Box] Box054  label="Cube014 Arduino Support cube001"
  Height = 67
  Length = 55
  Placement = pos=(-13,5,-68) rot=(0,0,1;0rad)
  Width = 5
FEATURE [Part::Box] Box055  label="Cube048"
  Height = 117
  Length = 33
  Placement = pos=(-46,7,-68) rot=(0,0,1;0rad)
  Width = 3
FEATURE [Part::Box] Box056  label="Cube049"
  Height = 117
  Length = 31
  Placement = pos=(42,7,-68) rot=(0,0,1;0rad)
  Width = 3
FEATURE [Part::Cylinder] Cylinder083  label="Cylinder179"
  Angle = 360
  Height = 28
  Placement = pos=(48,20,-10) rot=(1,0,0;1.5708rad)
  Radius = 1.6
FEATURE [Part::Cylinder] Cylinder084  label="Cylinder180"
  Angle = 360
  Height = 28
  Placement = pos=(48,20,-17) rot=(1,0,0;1.5708rad)
  Radius = 1.6
FEATURE [Part::Cylinder] Cylinder085  label="Cylinder181"
  Angle = 360
  Height = 28
  Placement = pos=(55,20,-17) rot=(1,0,0;1.5708rad)
  Radius = 1.6
FEATURE [Part::Cylinder] Cylinder086  label="Cylinder182"
  Angle = 360
  Height = 28
  Placement = pos=(55,20,-10) rot=(1,0,0;1.5708rad)
  Radius = 1.6
FEATURE [Part::MultiFuse] Fusion117  label="Mount holes top left001"
  Placement = pos=(-1,0,46) rot=(0,0,1;0rad)
  Shapes = -> [Cylinder084,Cylinder085,Cylinder086,Cylinder083]
FEATURE [Part::MultiFuse] Fusion118  label="Mount holes top right001"
  Placement = pos=(-71,0,46) rot=(0,0,1;0rad)
  Shapes = -> [Cylinder084,Cylinder085,Cylinder086,Cylinder083]
FEATURE [Part::Cylinder] Cylinder087  label="Cylinder183"
  Angle = 360
  Height = 10
  Placement = pos=(0,18,29) rot=(0,0,1;0rad)
  Radius = 2.25
FEATURE [Part::Cylinder] Cylinder088  label="Cylinder184"
  Angle = 360
  Height = 10
  Placement = pos=(4.5,18,32) rot=(0,0,1;0rad)
  Radius = 1
FEATURE [Part::Cylinder] Cylinder089  label="Cylinder185"
  Angle = 360
  Height = 10
  Placement = pos=(-4.5,18,32) rot=(0,0,1;0rad)
  Radius = 1
FEATURE [Part::Fuse] Fusion119  label="Mounting Screw Holes002"
  Base = -> Cylinder088
  Tool = -> Cylinder089
FEATURE [Part::Fuse] Fusion120  label="Motor Holes Left001"
  Base = -> Cylinder087
  Placement = pos=(37,-7,-3) rot=(0.57735,0.57735,0.57735;2.0944rad)
  Tool = -> Fusion119
FEATURE [Part::Cylinder] Cylinder090  label="Cylinder186"
  Angle = 360
  Height = 10
  Placement = pos=(0,18,29) rot=(0,0,1;0rad)
  Radius = 2.25
FEATURE [Part::Cylinder] Cylinder091  label="Cylinder187"
  Angle = 360
  Height = 10
  Placement = pos=(4.5,18,32) rot=(0,0,1;0rad)
  Radius = 1
FEATURE [Part::Cylinder] Cylinder092  label="Cylinder188"
  Angle = 360
  Height = 10
  Placement = pos=(-4.5,18,32) rot=(0,0,1;0rad)
  Radius = 1
FEATURE [Part::Fuse] Fusion121  label="Mounting Screw Holes003"
  Base = -> Cylinder091
  Tool = -> Cylinder092
FEATURE [Part::Fuse] Fusion122  label="Motor Holes Right001"
  Base = -> Cylinder090
  Placement = pos=(-79,-7,-3) rot=(0.57735,0.57735,0.57735;2.0944rad)
  Tool = -> Fusion121
FEATURE [Part::Cylinder] Cylinder093  label="Cylinder189"
  Angle = 360
  Height = 28
  Placement = pos=(40.7,0,-10.3) rot=(1,0,0;1.5708rad)
  Radius = 1.6
FEATURE [Part::Cylinder] Cylinder094  label="Cylinder190"
  Angle = 360
  Height = 28
  Placement = pos=(-2.4,0,-59.8) rot=(1,0,0;1.5708rad)
  Radius = 1.6
FEATURE [Part::Cylinder] Cylinder095  label="Cylinder191"
  Angle = 360
  Height = 28
  Placement = pos=(-5,0,-9) rot=(1,0,0;1.5708rad)
  Radius = 1.6
FEATURE [Part::Cylinder] Cylinder096  label="Cylinder192"
  Angle = 360
  Height = 28
  Placement = pos=(25.5,0,-59.8) rot=(1,0,0;1.5708rad)
  Radius = 1.6
FEATURE [Part::Fuse] Fusion123
  Base = -> Cylinder094
  Tool = -> Cylinder095
FEATURE [Part::Fuse] Fusion124
  Base = -> Cylinder093
  Tool = -> Cylinder096
FEATURE [Part::Fuse] Fusion125  label="Screw holes on Arduino Duo002"
  Base = -> Fusion123
  Tool = -> Fusion124
FEATURE [Part::Mirroring] Part__Mirroring006  label="Screw holes on Arduino Duo (Mirror #1)002"
  Base = (0,0,0)
  Normal = (0,0,1)
  Placement = pos=(-4,10,-67) rot=(0,0,1;0rad)
  Source = -> Fusion125
FEATURE [Part::Mirroring] Part__Mirroring007  label="Screw holes on Arduino Duo (Mirror #1)001 (Mirror #4)001"
  Base = (0,0,0)
  Normal = (1,0,0)
  Placement = pos=(27,0,-6) rot=(0,0,1;0rad)
  Source = -> Part__Mirroring006
FEATURE [Part::Box] Box057  label="Cube050"
  Height = 50
  Length = 47
  Placement = pos=(-9,-8,0) rot=(0,0,1;0rad)
  Width = 12
FEATURE [Part::Box] Box058  label="Cube051"
  Height = 55
  Length = 53
  Placement = pos=(-12,-8,-2.5) rot=(0,0,1;0rad)
  Width = 11
FEATURE [Part::Cut] Cut045029
  Base = -> Box058
  Tool = -> Box057
FEATURE [Part::Box] Box059  label="Cube052"
  Height = 5
  Length = 3
  Placement = pos=(35,-9,-4) rot=(0,0,1;0rad)
  Width = 12
FEATURE [Part::Cut] Cut045030
  Base = -> Cut045029
  Placement = pos=(-9,10,-58) rot=(1,0,0;1.5708rad)
  Tool = -> Box059
FEATURE [Part::Cut] Cut045031
  Base = -> Cut045029
  Placement = pos=(36.7,10,-56.7) rot=(1,0,0;1.5708rad)
  Tool = -> Box059
FEATURE [Part::Cut] Cut045032
  Base = -> Cut045029
  Placement = pos=(-6.4,10,-7.2) rot=(1,0,0;1.5708rad)
  Tool = -> Box059
FEATURE [Part::Cut] Cut045033
  Base = -> Cut045029
  Placement = pos=(21.5,10,-7.2) rot=(1,0,0;1.5708rad)
  Tool = -> Box059
FEATURE [Part::MultiFuse] Fusion126
  Shapes = -> [Cut045030,Cut045033,Cut045031,Cut045032]
FEATURE [Part::Mirroring] Part__Mirroring008  label="Hex Holes001"
  Base = (0,0,0)
  Normal = (1,0,0)
  Placement = pos=(27,0,-6) rot=(0,0,1;0rad)
  Source = -> Fusion126
FEATURE [Part::Box] Box060  label="Cube053"
  Height = 5
  Length = 2
  Placement = pos=(37.5,-9,-2) rot=(0,0,1;0rad)
  Width = 12
FEATURE [Part::Box] Box061  label="Battery Base001"
  Height = 50
  Length = 55
  Placement = pos=(-13,3,-1) rot=(0,0,1;0rad)
  Width = 7
FEATURE [Part::Cylinder] Cylinder097  label="Cylinder193"
  Angle = 360
  Height = 42
  Radius = 4.8
FEATURE [Part::Cylinder] Cylinder098  label="Cylinder194"
  Angle = 360
  Height = 1.6
  Placement = pos=(0,0,42) rot=(0,0,1;0rad)
  Radius = 1.65
FEATURE [Part::Fuse] Fusion127
  Base = -> Cylinder097
  Placement = pos=(2,0,0) rot=(0,0,1;0rad)
  Tool = -> Cylinder098
FEATURE [Part::Cylinder] Cylinder099  label="Cylinder195"
  Angle = 360
  Height = 42
  Radius = 4.8
FEATURE [Part::Cylinder] Cylinder100  label="Cylinder196"
  Angle = 360
  Height = 1.6
  Placement = pos=(0,0,42) rot=(0,0,1;0rad)
  Radius = 1.65
FEATURE [Part::Fuse] Fusion128
  Base = -> Cylinder099
  Placement = pos=(12,0,0) rot=(0,0,1;0rad)
  Tool = -> Cylinder100
FEATURE [Part::Cylinder] Cylinder101  label="Cylinder197"
  Angle = 360
  Height = 42
  Radius = 4.8
FEATURE [Part::Cylinder] Cylinder102  label="Cylinder198"
  Angle = 360
  Height = 1.6
  Placement = pos=(0,0,42) rot=(0,0,1;0rad)
  Radius = 1.65
FEATURE [Part::Fuse] Fusion129
  Base = -> Cylinder101
  Placement = pos=(22,0,0) rot=(0,0,1;0rad)
  Tool = -> Cylinder102
FEATURE [Part::Cylinder] Cylinder103  label="Cylinder199"
  Angle = 360
  Height = 42
  Radius = 4.8
FEATURE [Part::Cylinder] Cylinder104  label="Cylinder200"
  Angle = 360
  Height = 1.6
  Placement = pos=(0,0,42) rot=(0,0,1;0rad)
  Radius = 1.65
FEATURE [Part::Fuse] Fusion130
  Base = -> Cylinder103
  Placement = pos=(32,0,0) rot=(0,0,1;0rad)
  Tool = -> Cylinder104
FEATURE [Part::Cylinder] Cylinder105  label="Cylinder201"
  Angle = 360
  Height = 42
  Radius = 4.8
FEATURE [Part::Cylinder] Cylinder106  label="Cylinder202"
  Angle = 360
  Height = 1.6
  Placement = pos=(0,0,42) rot=(0,0,1;0rad)
  Radius = 1.65
FEATURE [Part::Fuse] Fusion131
  Base = -> Cylinder105
  Placement = pos=(-8,0,0) rot=(0,0,1;0rad)
  Tool = -> Cylinder106
FEATURE [Part::MultiFuse] Fusion132  label="AAA Batts002"
  Placement = pos=(2,0,2) rot=(0,0,1;0rad)
  Shapes = -> [Fusion131,Fusion127,Fusion128,Fusion129,Fusion130]
FEATURE [Part::Cut] Cut045034
  Base = -> Box061
  Tool = -> Fusion132
FEATURE [Part::Box] Box062  label="Cube054"
  Height = 2.5
  Length = 55
  Placement = pos=(-13,-9,-1) rot=(0,0,1;0rad)
  Width = 12
FEATURE [Part::Box] Box063  label="Cube055"
  Height = 2.5
  Length = 55
  Placement = pos=(-13,-9,46.5) rot=(0,0,1;0rad)
  Width = 12
FEATURE [Part::Box] Box064  label="Cube056"
  Height = 50
  Length = 2.5
  Placement = pos=(-13,-9,-1) rot=(0,0,1;0rad)
  Width = 12
FEATURE [Part::Box] Box065  label="Cube057"
  Height = 50
  Length = 2.5
  Placement = pos=(39.5,-9,-1) rot=(0,0,1;0rad)
  Width = 12
FEATURE [Part::MultiFuse] Fusion133
  Shapes = -> [Box062,Box064,Box065,Box063]
FEATURE [Part::Box] Box066  label="Cube058"
  Height = 5
  Length = 2
  Placement = pos=(-10.5,-9,46) rot=(0,0,1;0rad)
  Width = 12
FEATURE [Part::Box] Box067  label="Cube059"
  Height = 5
  Length = 2
  Placement = pos=(-10.5,-9,-2) rot=(0,0,1;0rad)
  Width = 12
FEATURE [Part::MultiFuse] Fusion134
  Shapes = -> [Box067,Box066,Box060,Box048]
FEATURE [Part::MultiFuse] Fusion135
  Shapes = -> [Box045,Box046,Box047,Box049]
FEATURE [Part::Cut] Cut045035
  Base = -> Fusion133
  Tool = -> Fusion134
FEATURE [Part::Cut] Cut045036
  Base = -> Cut045035
  Tool = -> Fusion135
FEATURE [Part::Cylinder] Cylinder107  label="Cylinder203"
  Angle = 360
  Height = 14.5
  Placement = pos=(-43.6,-2.4,-15) rot=(0,0,1;0rad)
  Radius = 0.8
FEATURE [Part::Cylinder] Cylinder108  label="Cylinder204"
  Angle = 360
  Height = 14.5
  Placement = pos=(-43.6,-13.8,-15) rot=(0,0,1;0rad)
  Radius = 0.8
FEATURE [Part::Fuse] Fusion136
  Base = -> Cut045034
  Tool = -> Cut045036
FEATURE [Part::Box] Box068  label="Cube060"
  Height = 4
  Length = 12
  Placement = pos=(-50,-16.75,-14) rot=(0,0,1;0rad)
  Width = 26.75
FEATURE [Part::Chamfer] Chamfer002
  Base = -> Box068
  Edges = 1 edges r=7: [Edge3]
FEATURE [Part::Cone] Cone004
  Angle = 360
  Height = 1.5
  Placement = pos=(-43.6,-2.4,-10) rot=(0,0,1;0rad)
  Radius1 = 2.75
  Radius2 = 1.25
FEATURE [Part::Cone] Cone005
  Angle = 360
  Height = 1.5
  Placement = pos=(-43.6,-13.8,-10) rot=(0,0,1;0rad)
  Radius1 = 2.75
  Radius2 = 1.25
FEATURE [Part::Fuse] Fusion137
  Base = -> Cone004
  Tool = -> Cone005
FEATURE [Part::Fuse] Fusion138
  Base = -> Chamfer002
  Tool = -> Fusion137
FEATURE [Part::Fuse] Fusion139
  Base = -> Cylinder107
  Tool = -> Cylinder108
FEATURE [Part::Cut] Cut045037
  Base = -> Fusion138
  Tool = -> Fusion139
FEATURE [Part::Cylinder] Cylinder109  label="Cylinder205"
  Angle = 360
  Height = 14.5
  Placement = pos=(-43.6,-2.4,-15) rot=(0,0,1;0rad)
  Radius = 0.8
FEATURE [Part::Cylinder] Cylinder110  label="Cylinder206"
  Angle = 360
  Height = 14.5
  Placement = pos=(-43.6,-13.8,-15) rot=(0,0,1;0rad)
  Radius = 0.8
FEATURE [Part::Box] Box069  label="Cube061"
  Height = 4
  Length = 12
  Placement = pos=(-50,-16.75,-14) rot=(0,0,1;0rad)
  Width = 26.75
FEATURE [Part::Chamfer] Chamfer003
  Base = -> Box069
  Edges = 1 edges r=7: [Edge3]
FEATURE [Part::Cone] Cone006
  Angle = 360
  Height = 1.5
  Placement = pos=(-43.6,-2.4,-10) rot=(0,0,1;0rad)
  Radius1 = 2.75
  Radius2 = 1.25
FEATURE [Part::Cone] Cone007
  Angle = 360
  Height = 1.5
  Placement = pos=(-43.6,-13.8,-10) rot=(0,0,1;0rad)
  Radius1 = 2.75
  Radius2 = 1.25
FEATURE [Part::Fuse] Fusion140
  Base = -> Cone006
  Tool = -> Cone007
FEATURE [Part::Fuse] Fusion141
  Base = -> Chamfer003
  Tool = -> Fusion140
FEATURE [Part::Fuse] Fusion142
  Base = -> Cylinder109
  Tool = -> Cylinder110
FEATURE [Part::Cut] Cut045038
  Base = -> Fusion141
  Tool = -> Fusion142
FEATURE [Part::Mirroring] Part__Mirroring009  label="Cut045028 (Mirror #6)001"
  Base = (0,0,0)
  Normal = (1,0,0)
  Placement = pos=(27,0,0) rot=(0,0,1;0rad)
  Source = -> Cut045038
FEATURE [Part::Cut] Cut045039
  Base = -> Box050
  Tool = -> Fusion120
FEATURE [Part::Cut] Cut045040
  Base = -> Box051
  Tool = -> Fusion122
FEATURE [Part::MultiFuse] Fusion143
  Shapes = -> [Box054,Box055,Box056]
FEATURE [Part::Fuse] Fusion144
  Base = -> Fusion136
  Tool = -> Fusion143
FEATURE [Part::MultiFuse] Fusion145
  Shapes = -> [Fusion144,Cut045040,Cut045039]
FEATURE [Part::MultiFuse] Fusion146
  Shapes = -> [Fusion145,Part__Mirroring009,Cut045037]
FEATURE [Part::Cut] Cut045041
  Base = -> Fusion146
  Tool = -> Fusion117
FEATURE [Part::Cut] Cut045042
  Base = -> Cut045041
  Tool = -> Fusion118
FEATURE [Part::Cut] Cut045043
  Base = -> Cut045042
  Tool = -> Part__Mirroring007
FEATURE [Part::Cut] Cut045044
  Base = -> Cut045043
  Tool = -> Part__Mirroring008
FEATURE [Part::MultiFuse] Fusion147
  Shapes = -> [Cut045044,Box053,Box052]
FEATURE [Part::Chamfer] Chamfer004
  Base = -> Fusion147
  Edges = 1 edges r=25: [Edge43]
FEATURE [Part::Chamfer] Chamfer005
  Base = -> Chamfer004
  Edges = 1 edges r=25: [Edge225]
FEATURE [Part::Chamfer] Chamfer006
  Base = -> Chamfer005
  Edges = 1 edges r=30: [Edge58]
FEATURE [Part::Chamfer] Chamfer007
  Base = -> Chamfer006
  Edges = 1 edges r=30: [Edge148]
FEATURE [Part::Fillet] Fillet
  Base = -> Chamfer007
  Edges = 1 edges r=2: [Edge233]
FEATURE [Part::Fillet] Fillet001
  Base = -> Fillet
  Edges = 1 edges r=2: [Edge6]
FEATURE [Part::Fillet] Fillet002
  Base = -> Fillet001
  Edges = 1 edges r=2: [Edge2]
FEATURE [Part::Fillet] Fillet003
  Base = -> Fillet002
  Edges = 1 edges r=2: [Edge357]
FEATURE [Part::Fillet] Fillet004
  Base = -> Fillet003
  Edges = 1 edges r=2: [Edge6]
FEATURE [Part::Fillet] Fillet005
  Base = -> Fillet004
  Edges = 1 edges r=2: [Edge2]
FEATURE [Part::Fillet] Fillet006
  Base = -> Fillet005
  Edges = 1 edges r=2: [Edge407]
FEATURE [Part::Fillet] Fillet007
  Base = -> Fillet006
  Edges = 1 edges r=2: [Edge2]
FEATURE [Part::Fillet] Fillet008
  Base = -> Fillet007
  Edges = 1 edges r=2: [Edge369]
FEATURE [Part::Fillet] Fillet009
  Base = -> Fillet008
  Edges = 1 edges r=2: [Edge2]
FEATURE [Part::Cylinder] Cylinder111  label="Cylinder207"
  Angle = 360
  Height = 28
  Placement = pos=(45,6,47) rot=(0.707107,0,0.707107;4.01426rad)
  Radius = 0.5
FEATURE [Part::Cylinder] Cylinder112  label="Cylinder208"
  Angle = 360
  Height = 28
  Placement = pos=(66,6,26) rot=(0.707107,0,0.707107;4.01426rad)
  Radius = 0.5
FEATURE [Part::Cut] Cut045045
  Base = -> Fillet009
  Tool = -> Cylinder111
FEATURE [Part::Cut] Cut045046
  Base = -> Cut045045
  Tool = -> Cylinder112
FEATURE [Part::Cylinder] Cylinder113  label="Cylinder209"
  Angle = 360
  Height = 28
  Placement = pos=(66,6,26) rot=(0.707107,0,0.707107;4.01426rad)
  Radius = 0.5
FEATURE [Part::Mirroring] Part__Mirroring010  label="Cylinder137 (Mirror #7)"
  Base = (0,0,0)
  Normal = (1,0,0)
  Placement = pos=(27,0,0) rot=(0,0,1;0rad)
  Source = -> Cylinder113
FEATURE [Part::Cylinder] Cylinder114  label="Cylinder210"
  Angle = 360
  Height = 28
  Placement = pos=(45,6,47) rot=(0.707107,0,0.707107;4.01426rad)
  Radius = 0.5
FEATURE [Part::Mirroring] Part__Mirroring011  label="Cylinder138 (Mirror #8)"
  Base = (0,0,0)
  Normal = (1,0,0)
  Placement = pos=(27,0,0) rot=(0,0,1;0rad)
  Source = -> Cylinder114
FEATURE [Part::Cut] Cut045047
  Base = -> Cut045046
  Tool = -> Part__Mirroring010
FEATURE [Part::Cut] Cut045048
  Base = -> Cut045047
  Tool = -> Part__Mirroring011
FEATURE [App::DocumentObjectGroup] Group  label="Older version parts"
  Group = -> [Compound,Compound001,Compound002,Cylinder064,Cylinder010,Cylinder011,Fusion096,Part__Mirroring,Fusion054,Part__Mirroring004,Cut014,Cut015,Cut016,Cut017,Cut045048,Part__Mirroring003]
FEATURE [Part::Cylinder] Cylinder115  label="Arduino Cylinder191"
  Angle = 360
  Height = 28
  Placement = pos=(4,11,-8.6) rot=(1,0,0;1.5708rad)
  Radius = 1.6
FEATURE [Part::Cylinder] Cylinder116  label="Arduino Cylinder192"
  Angle = 360
  Height = 28
  Placement = pos=(31.9,11,-8.6) rot=(1,0,0;1.5708rad)
  Radius = 1.6
FEATURE [Part::Cylinder] Cylinder117  label="Arduino Cylinder193"
  Angle = 360
  Height = 28
  Placement = pos=(-11.2,11,-59.4) rot=(1,0,0;1.5708rad)
  Radius = 1.6
FEATURE [Part::Cylinder] Cylinder118  label="Arduino Cylinder194"
  Angle = 360
  Height = 28
  Placement = pos=(37,11,-60.7) rot=(1,0,0;1.5708rad)
  Radius = 1.6
FEATURE [Part::Cylinder] Cylinder119  label="Arduino Cylinder195"
  Angle = 360
  Height = 2.5
  Placement = pos=(4,13,-8.6) rot=(1,0,0;1.5708rad)
  Radius = 4
FEATURE [Part::Feature] Box014001
  Placement = pos=(3.88157,4,-2.89487) rot=(0,1,0;1.0472rad)
  shape: bbox 13.66 x 10 x 13.66 mm, 6 faces (baked)
FEATURE [Part::Feature] Box014002
  Placement = pos=(8.88157,4,-5.64487) rot=(0,1,0;2.0944rad)
  shape: bbox 13.66 x 10 x 13.66 mm, 6 faces (baked)
FEATURE [Part::Feature] Box014003
  Placement = pos=(9,4,-11.35) rot=(0,1,0;3.14159rad)
  shape: bbox 10 x 10 x 10 mm, 6 faces (baked)
FEATURE [Part::Feature] Box014004
  Placement = pos=(4.11843,4,-14.3051) rot=(0,1,0;4.18879rad)
  shape: bbox 13.66 x 10 x 13.66 mm, 6 faces (baked)
FEATURE [Part::Feature] Box014005
  Placement = pos=(-0.88157,4,-11.5551) rot=(0,-1,0;1.0472rad)
  shape: bbox 13.66 x 10 x 13.66 mm, 6 faces (baked)
FEATURE [Part::MultiFuse] Fusion148
  Shapes = -> [Box014001,Box014002,Box014004,Box014003,Box014005,Box014]
FEATURE [Part::Cut] Cut045049  label="M3 Nut004"
  Base = -> Cylinder119
  Placement = pos=(0,-3,0) rot=(0,0,1;0rad)
  Tool = -> Fusion148
FEATURE [Part::Box] Box014006  label="Not used Cube001"
  Height = 10
  Length = 10
  Placement = pos=(-1,4,-5.85) rot=(0,0,1;0rad)
  Width = 10
FEATURE [Part::Cylinder] Cylinder120  label="Arduino Cylinder196"
  Angle = 360
  Height = 2.5
  Placement = pos=(4,13,-8.6) rot=(1,0,0;1.5708rad)
  Radius = 4
FEATURE [Part::Feature] Box014007
  Placement = pos=(3.88157,4,-2.89487) rot=(0,1,0;1.0472rad)
  shape: bbox 13.66 x 10 x 13.66 mm, 6 faces (baked)
FEATURE [Part::Feature] Box014008
  Placement = pos=(8.88157,4,-5.64487) rot=(0,1,0;2.0944rad)
  shape: bbox 13.66 x 10 x 13.66 mm, 6 faces (baked)
FEATURE [Part::Feature] Box014009
  Placement = pos=(9,4,-11.35) rot=(0,1,0;3.14159rad)
  shape: bbox 10 x 10 x 10 mm, 6 faces (baked)
FEATURE [Part::Feature] Box014010
  Placement = pos=(4.11843,4,-14.3051) rot=(0,1,0;4.18879rad)
  shape: bbox 13.66 x 10 x 13.66 mm, 6 faces (baked)
FEATURE [Part::Feature] Box014011
  Placement = pos=(-0.88157,4,-11.5551) rot=(0,-1,0;1.0472rad)
  shape: bbox 13.66 x 10 x 13.66 mm, 6 faces (baked)
FEATURE [Part::MultiFuse] Fusion149
  Shapes = -> [Box014007,Box014008,Box014010,Box014009,Box014011,Box014006]
FEATURE [Part::Cut] Cut045050  label="M3 Nut005"
  Base = -> Cylinder120
  Placement = pos=(27.9,-3,0) rot=(0,0,1;0rad)
  Tool = -> Fusion149
FEATURE [Part::Box] Box014012  label="Not used Cube002"
  Height = 10
  Length = 10
  Placement = pos=(-1,4,-5.85) rot=(0,0,1;0rad)
  Width = 10
FEATURE [Part::Cylinder] Cylinder121  label="Arduino Cylinder197"
  Angle = 360
  Height = 2.5
  Placement = pos=(4,13,-8.6) rot=(1,0,0;1.5708rad)
  Radius = 4
FEATURE [Part::Feature] Box014013
  Placement = pos=(3.88157,4,-2.89487) rot=(0,1,0;1.0472rad)
  shape: bbox 13.66 x 10 x 13.66 mm, 6 faces (baked)
FEATURE [Part::Feature] Box014014
  Placement = pos=(8.88157,4,-5.64487) rot=(0,1,0;2.0944rad)
  shape: bbox 13.66 x 10 x 13.66 mm, 6 faces (baked)
FEATURE [Part::Feature] Box014015
  Placement = pos=(9,4,-11.35) rot=(0,1,0;3.14159rad)
  shape: bbox 10 x 10 x 10 mm, 6 faces (baked)
FEATURE [Part::Feature] Box014016
  Placement = pos=(4.11843,4,-14.3051) rot=(0,1,0;4.18879rad)
  shape: bbox 13.66 x 10 x 13.66 mm, 6 faces (baked)
FEATURE [Part::Feature] Box014017
  Placement = pos=(-0.88157,4,-11.5551) rot=(0,-1,0;1.0472rad)
  shape: bbox 13.66 x 10 x 13.66 mm, 6 faces (baked)
FEATURE [Part::MultiFuse] Fusion150
  Shapes = -> [Box014013,Box014014,Box014016,Box014015,Box014017,Box014012]
FEATURE [Part::Cut] Cut045051  label="M3 Nut006"
  Base = -> Cylinder121
  Placement = pos=(-15.2,-3,-50.8) rot=(0,0,1;0rad)
  Tool = -> Fusion150
FEATURE [Part::Box] Box014018  label="Not used Cube003"
  Height = 10
  Length = 10
  Placement = pos=(-1,4,-5.85) rot=(0,0,1;0rad)
  Width = 10
FEATURE [Part::Cylinder] Cylinder122  label="Arduino Cylinder198"
  Angle = 360
  Height = 2.5
  Placement = pos=(4,13,-8.6) rot=(1,0,0;1.5708rad)
  Radius = 4
FEATURE [Part::Feature] Box014019
  Placement = pos=(3.88157,4,-2.89487) rot=(0,1,0;1.0472rad)
  shape: bbox 13.66 x 10 x 13.66 mm, 6 faces (baked)
FEATURE [Part::Feature] Box014020
  Placement = pos=(8.88157,4,-5.64487) rot=(0,1,0;2.0944rad)
  shape: bbox 13.66 x 10 x 13.66 mm, 6 faces (baked)
FEATURE [Part::Feature] Box014021
  Placement = pos=(9,4,-11.35) rot=(0,1,0;3.14159rad)
  shape: bbox 10 x 10 x 10 mm, 6 faces (baked)
FEATURE [Part::Feature] Box014022
  Placement = pos=(4.11843,4,-14.3051) rot=(0,1,0;4.18879rad)
  shape: bbox 13.66 x 10 x 13.66 mm, 6 faces (baked)
FEATURE [Part::Feature] Box014023
  Placement = pos=(-0.88157,4,-11.5551) rot=(0,-1,0;1.0472rad)
  shape: bbox 13.66 x 10 x 13.66 mm, 6 faces (baked)
FEATURE [Part::MultiFuse] Fusion151
  Shapes = -> [Box014019,Box014020,Box014022,Box014021,Box014023,Box014018]
FEATURE [Part::Cut] Cut045052  label="M3 Nut007"
  Base = -> Cylinder122
  Placement = pos=(33,-3,-52.1) rot=(0,0,1;0rad)
  Tool = -> Fusion151
FEATURE [Part::Box] Box014024  label="Cube062"
  Height = 67
  Length = 65
  Placement = pos=(-16,-13,-6) rot=(0,0,1;0rad)
  Width = 8
FEATURE [Part::Cut] Cut045053  label="BAtt Holder"
  Base = -> Fusion110
  Tool = -> Box014024
FEATURE [Part::Cylinder] Cylinder123  label="Cylinder211"
  Angle = 360
  Height = 28
  Placement = pos=(45,6,47) rot=(0.707107,0,0.707107;4.01426rad)
  Radius = 0.5
FEATURE [Part::Cylinder] Cylinder124  label="Cylinder212"
  Angle = 360
  Height = 28
  Placement = pos=(66,6,26) rot=(0.707107,0,0.707107;4.01426rad)
  Radius = 0.5
FEATURE [Part::Cylinder] Cylinder125  label="Cylinder213"
  Angle = 360
  Height = 28
  Placement = pos=(45,6,47) rot=(0.707107,0,0.707107;4.01426rad)
  Radius = 0.5
FEATURE [Part::Cylinder] Cylinder126  label="Cylinder214"
  Angle = 360
  Height = 28
  Placement = pos=(66,6,26) rot=(0.707107,0,0.707107;4.01426rad)
  Radius = 0.5
FEATURE [Part::Mirroring] Part__Mirroring012  label="Cylinder211 (Mirror #13)"
  Base = (0,0,0)
  Normal = (1,0,0)
  Placement = pos=(27,0,0) rot=(0,0,1;0rad)
  Source = -> Cylinder125
FEATURE [Part::Mirroring] Part__Mirroring013  label="Cylinder212 (Mirror #14)"
  Base = (0,0,0)
  Normal = (1,0,0)
  Placement = pos=(27,0,0) rot=(0,0,1;0rad)
  Source = -> Cylinder126
FEATURE [Part::MultiFuse] Fusion152
  Shapes = -> [Box015,Box016,Box017]
FEATURE [Part::Chamfer] Chamfer008
  Base = -> Fusion152
  Edges = 1 edges r=25: [Edge3]
FEATURE [Part::Chamfer] Chamfer009
  Base = -> Chamfer008
  Edges = 1 edges r=25: [Edge42]
FEATURE [Part::Chamfer] Chamfer010
  Base = -> Chamfer009
  Edges = 1 edges r=30: [Edge9]
FEATURE [Part::Chamfer] Chamfer011
  Base = -> Chamfer010
  Edges = 1 edges r=30: [Edge42]
FEATURE [Part::Fuse] Fusion153
  Base = -> Cut045053
  Tool = -> Chamfer011
FEATURE [Part::Fuse] Fusion154  label="Mounts for wheel sensor"
  Base = -> Cut045027
  Tool = -> Part__Mirroring005
FEATURE [Part::Fuse] Fusion155
  Base = -> Fusion153
  Tool = -> Fusion154
FEATURE [Part::Fillet] Fillet010
  Base = -> Fusion155
  Edges = 1 edges r=1: [Edge128]
FEATURE [Part::Fillet] Fillet011
  Base = -> Fillet010
  Edges = 1 edges r=1: [Edge6]
FEATURE [Part::Fillet] Fillet012
  Base = -> Fillet011
  Edges = 1 edges r=1: [Edge2]
FEATURE [Part::Fillet] Fillet013
  Base = -> Fillet012
  Edges = 1 edges r=1: [Edge270]
FEATURE [Part::Fillet] Fillet014
  Base = -> Fillet013
  Edges = 1 edges r=1: [Edge6]
FEATURE [Part::Fillet] Fillet015
  Base = -> Fillet014
  Edges = 1 edges r=1: [Edge2]
FEATURE [Part::MultiFuse] Fusion156
  Shapes = -> [Part__Mirroring012,Part__Mirroring013,Cylinder124,Cylinder123]
FEATURE [Part::Cut] Cut045054
  Base = -> Fillet015
  Tool = -> Fusion156
FEATURE [Part::MultiFuse] Fusion157  label="Motor Support and mounts"
  Shapes = -> [Box010,Box011,Box012,Box013]
FEATURE [Part::Fuse] Fusion158
  Base = -> Cut045054
  Tool = -> Fusion157
FEATURE [Part::Cut] Cut045055
  Base = -> Fusion158
  Tool = -> Fusion057
FEATURE [Part::Cut] Cut045056
  Base = -> Cut045055
  Tool = -> Fusion058
FEATURE [Part::Cut] Cut045057
  Base = -> Cut045056
  Tool = -> Fusion071
FEATURE [Part::Cut] Cut045058
  Base = -> Cut045057
  Tool = -> Fusion073
FEATURE [Part::MultiFuse] Fusion159  label="Arduino mount holes"
  Shapes = -> [Cylinder115,Cylinder118,Cylinder117,Cylinder116]
FEATURE [Part::Cut] Cut045059
  Base = -> Cut045058
  Tool = -> Fusion159
FEATURE [Part::MultiFuse] Fusion160  label="M3 Nuts"
  Shapes = -> [Cut045052,Cut045049,Cut045050,Cut045051]
FEATURE [Part::Cut] Cut045060  label="Frank Main Body"
  Base = -> Cut045059
  Tool = -> Fusion160
